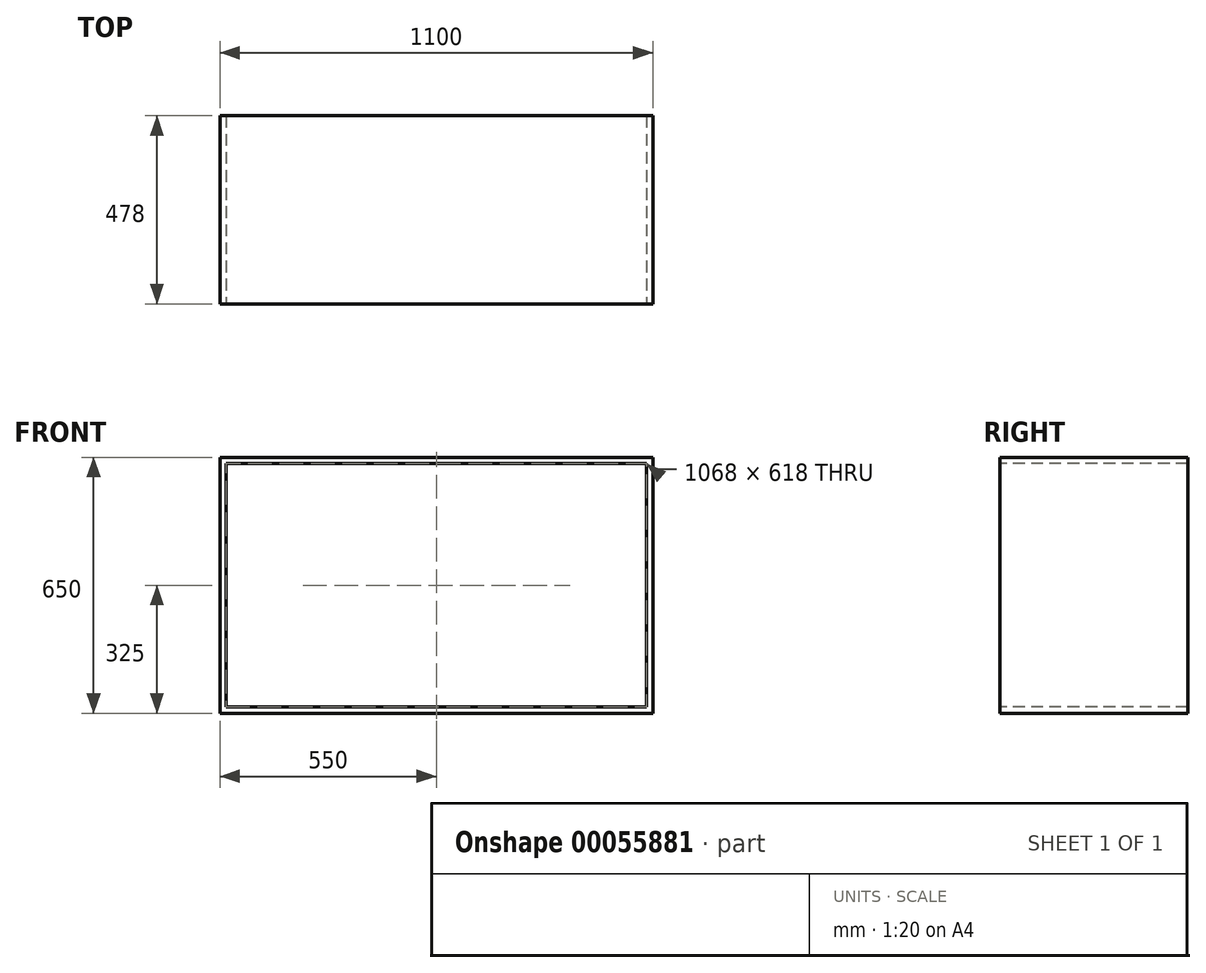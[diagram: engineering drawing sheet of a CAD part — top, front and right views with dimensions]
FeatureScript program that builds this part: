
annotation { "Feature Type Name" : "Feature", "Feature Type Description" : "" }
export const myFeature = defineFeature(function(context is Context, id is Id, definition is map)
    precondition{}
    {
        {
            var Q0;
            Q0=qCreatedBy(makeId("Front.planeOp"),FACE);
            var sketch = newSketch(context, id + "F0", { "sketchPlane" : qUnion([Q0])});
            skLineSegment(sketch, "E0.rect.bottom", {"start": v(-550, 325) * mm, "end": v(550, 325) * mm});
            skLineSegment(sketch, "E0.rect.top", {"start": v(-550, -325) * mm, "end": v(550, -325) * mm});
            skLineSegment(sketch, "E0.rect.left", {"start": v(-550, 325) * mm, "end": v(-550, -325) * mm});
            skLineSegment(sketch, "E0.rect.right", {"start": v(550, 325) * mm, "end": v(550, -325) * mm});
            skPoint(sketch, "E0.rect.middle", {"position": v(0, 0) * mm});
            skLineSegment(sketch, "E1.0", {"start": v(-534, 309) * mm, "end": v(534, 309) * mm});
            skLineSegment(sketch, "E1.1", {"start": v(-534, 309) * mm, "end": v(-534, -309) * mm});
            skLineSegment(sketch, "E1.2", {"start": v(-534, -309) * mm, "end": v(534, -309) * mm});
            skLineSegment(sketch, "E1.3", {"start": v(534, 309) * mm, "end": v(534, -309) * mm});
            skLineSegment(sketch, "E2", {"start": v(-234, 309) * mm, "end": v(-234, -309) * mm});
            skLineSegment(sketch, "E3", {"start": v(234, 309) * mm, "end": v(234, -309) * mm});
            skLineSegment(sketch, "E4.0", {"start": v(-218, 309) * mm, "end": v(-218, -309) * mm});
            skLineSegment(sketch, "E5.0", {"start": v(218, 309) * mm, "end": v(218, -309) * mm});
            skLineSegment(sketch, "E6", {"start": v(-534, 103) * mm, "end": v(-234, 103) * mm});
            skLineSegment(sketch, "E7", {"start": v(-534, -103) * mm, "end": v(-234, -103) * mm});
            skLineSegment(sketch, "E8", {"start": v(234, 103) * mm, "end": v(534, 103) * mm});
            skLineSegment(sketch, "E9", {"start": v(234, -103) * mm, "end": v(534, -103) * mm});
            skLineSegment(sketch, "E10", {"start": v(-202, 309) * mm, "end": v(-202, -309) * mm});
            skLineSegment(sketch, "E11", {"start": v(202, 309) * mm, "end": v(202, -309) * mm});
            skSolve(sketch);
        }
        {
            var Q0;
            Q0=qSketchRegion(id+"F0",true);
            extrude(context, id + "F1", {"entities" : qUnion([Q0]), "oppositeDirection" : true, "depth" : (500 - 22) * mm});
        }
    });
